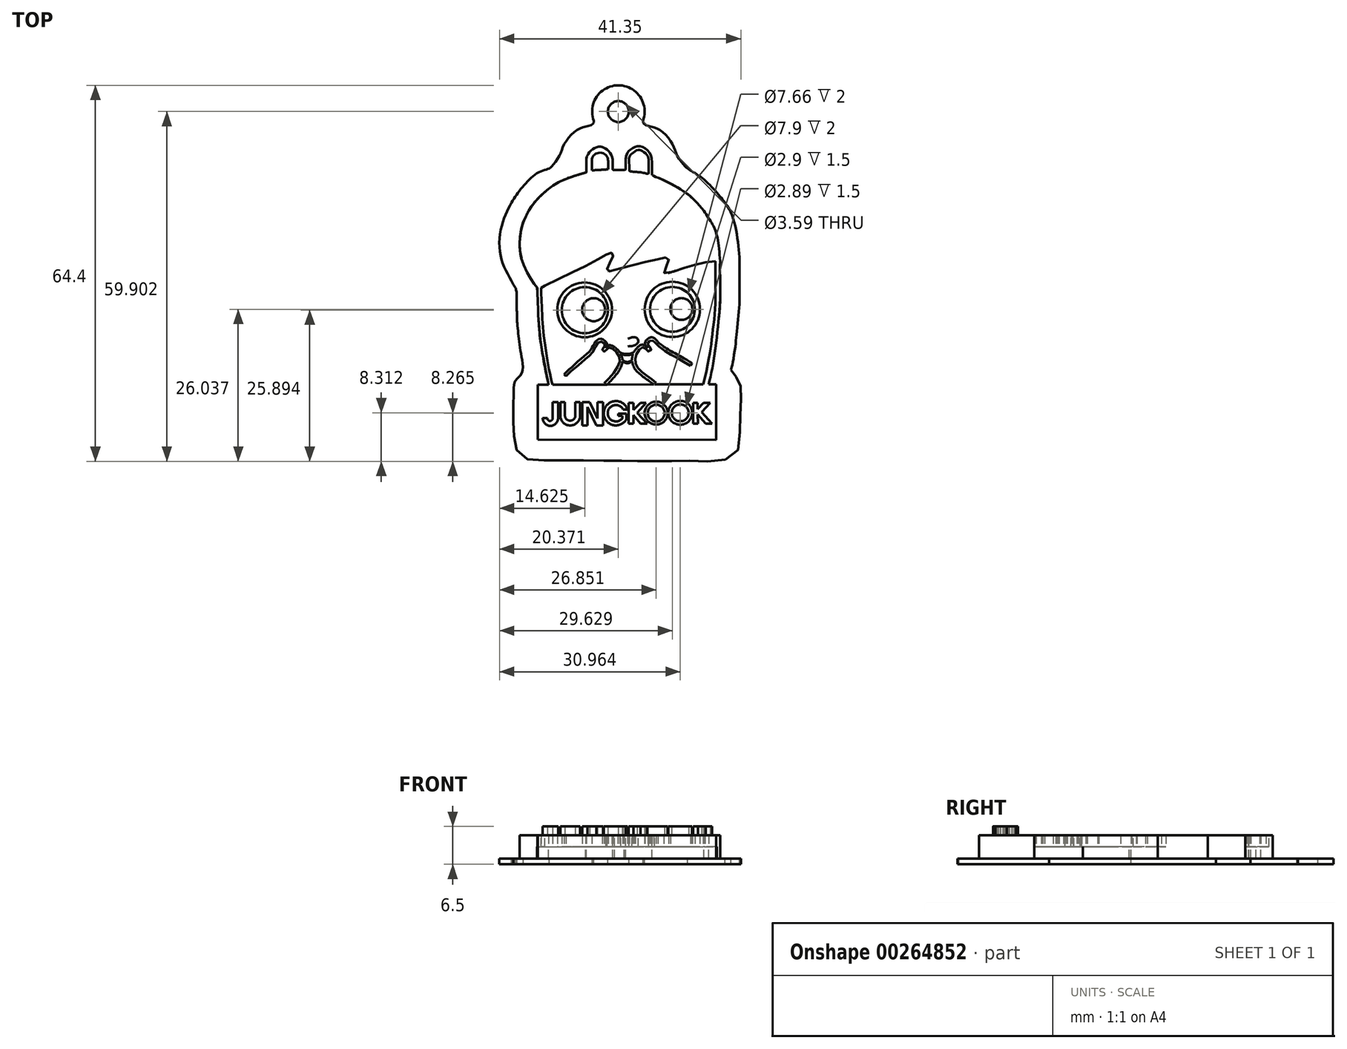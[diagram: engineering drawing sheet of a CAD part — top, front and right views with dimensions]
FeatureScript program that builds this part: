
annotation { "Feature Type Name" : "Feature", "Feature Type Description" : "" }
export const myFeature = defineFeature(function(context is Context, id is Id, definition is map)
    precondition{}
    {
        {
            var Q0;
            Q0=qCreatedBy(makeId("Top.planeOp"),FACE);
            var sketch = newSketch(context, id + "F0", { "sketchPlane" : qUnion([Q0])});
            skFitSpline(sketch, "E0", {"points": [v(-15.44, 3.8) * mm, v(-15.4, 3.06) * mm, v(-15.31, 1.12) * mm, v(-15.25, -0.63) * mm, v(-15.09, -3.15) * mm, v(-14.76, -5.82) * mm, v(-14.35, -8.3) * mm, v(-13.98, -10.2) * mm, v(-13.5, -12.48) * mm], "startDerivative": vector(0.66, -8.16) * mm, "endDerivative": vector(3.78, -17.47) * mm});
            skFitSpline(sketch, "E1", {"points": [v(-15.44, 3.8) * mm, v(-15.44, 4.09) * mm], "startDerivative": vector(0, 0.28) * mm, "endDerivative": vector(0, 0.28) * mm});
            skFitSpline(sketch, "E2", {"points": [v(-15.44, 4.09) * mm, v(-16.52, 5.66) * mm, v(-18.07, 8.9) * mm, v(-18.43, 11.83) * mm, v(-17.94, 15) * mm, v(-16.82, 17.42) * mm, v(-15.44, 19.28) * mm, v(-12.8, 21.53) * mm, v(-10.76, 22.67) * mm, v(-8.3, 23.5) * mm, v(-7.13, 23.85) * mm], "startDerivative": vector(-11.92, 16.14) * mm, "endDerivative": vector(15.07, 4.4) * mm});
            skFitSpline(sketch, "E3", {"points": [v(-7.13, 23.85) * mm, v(-7.03, 23.89) * mm, v(-7, 24.06) * mm], "startDerivative": vector(0.27, 0.05) * mm, "endDerivative": vector(0, 0.36) * mm});
            skFitSpline(sketch, "E4", {"points": [v(-7, 24.06) * mm, v(-7, 25.6) * mm, v(-7, 26.32) * mm], "startDerivative": vector(0, 2.86) * mm, "endDerivative": vector(0, 1.67) * mm});
            skFitSpline(sketch, "E5", {"points": [v(-7, 26.32) * mm, v(-6.88, 26.67) * mm, v(-6.59, 27.18) * mm, v(-5.88, 27.86) * mm, v(-5.1, 28.23) * mm, v(-4.41, 28.24) * mm, v(-3.8, 27.96) * mm, v(-3.14, 27.44) * mm, v(-2.64, 26.6) * mm, v(-2.5, 25.5) * mm], "startDerivative": vector(0.43, 2.5) * mm, "endDerivative": vector(0.33, -8.37) * mm});
            skFitSpline(sketch, "E6", {"points": [v(-2.5, 25.5) * mm, v(-2.5, 24.6) * mm], "startDerivative": vector(0, -0.9) * mm, "endDerivative": vector(0, -0.9) * mm});
            skFitSpline(sketch, "E7", {"points": [v(-2.5, 24.6) * mm, v(-2.45, 24.3) * mm, v(-2.22, 24.27) * mm], "startDerivative": vector(-0.02, -0.7) * mm, "endDerivative": vector(0.6, 0.05) * mm});
            skFitSpline(sketch, "E8", {"points": [v(-2.22, 24.27) * mm, v(-1.57, 24.27) * mm, v(-0.56, 24.27) * mm], "startDerivative": vector(1.37, 0) * mm, "endDerivative": vector(1.92, 0) * mm});
            skFitSpline(sketch, "E9", {"points": [v(-0.56, 24.27) * mm, v(-0.37, 24.31) * mm, v(-0.3, 24.69) * mm, v(-0.3, 25.35) * mm, v(-0.28, 26.2) * mm, v(0, 27.16) * mm, v(0.46, 27.7) * mm, v(0.96, 28.04) * mm, v(1.54, 28.27) * mm, v(2.25, 28.31) * mm, v(3.02, 27.97) * mm, v(3.65, 27.4) * mm, v(4.1, 26.52) * mm, v(4.2, 25.06) * mm, v(4.21, 23.66) * mm], "startDerivative": vector(6.4, 0.3) * mm, "endDerivative": vector(0.05, -13.65) * mm});
            skFitSpline(sketch, "E10", {"points": [v(4.21, 23.66) * mm, v(4.21, 23.5) * mm, v(4.44, 23.27) * mm, v(5.7, 22.76) * mm, v(7.7, 21.78) * mm, v(9.76, 20.54) * mm, v(11.37, 19.22) * mm, v(13.08, 17.27) * mm], "startDerivative": vector(-0.74, -3.46) * mm, "endDerivative": vector(8.63, -10.7) * mm});
            skFitSpline(sketch, "E11", {"points": [v(13.08, 17.27) * mm, v(14.13, 15.74) * mm, v(14.87, 14.38) * mm, v(15.47, 12.46) * mm, v(15.87, 8.68) * mm], "startDerivative": vector(4.76, -6.59) * mm, "endDerivative": vector(0.64, -11.93) * mm});
            skFitSpline(sketch, "E12", {"points": [v(15.87, 8.68) * mm, v(15.87, 5.96) * mm, v(15.87, 1.45) * mm, v(15.63, -1.38) * mm, v(15.33, -4.13) * mm], "startDerivative": vector(-0.06, -11.86) * mm, "endDerivative": vector(-1.6, -12.17) * mm});
            skFitSpline(sketch, "E13", {"points": [v(15.33, -4.13) * mm, v(15, -6.79) * mm, v(14.65, -9.15) * mm, v(14.27, -10.95) * mm, v(13.93, -12.45) * mm], "startDerivative": vector(-1, -9.39) * mm, "endDerivative": vector(-0.83, -6.4) * mm});
            skLineSegment(sketch, "E14", {"start": v(13.93, -12.45) * mm, "end": v(15.17, -12.45) * mm});
            skLineSegment(sketch, "E15", {"start": v(15.17, -12.45) * mm, "end": v(15.17, -21.93) * mm});
            skLineSegment(sketch, "E16", {"start": v(-15.34, -12.48) * mm, "end": v(-13.5, -12.48) * mm});
            skLineSegment(sketch, "E17", {"start": v(-15.34, -12.48) * mm, "end": v(-15.34, -21.89) * mm});
            skLineSegment(sketch, "E18", {"start": v(-15.34, -21.89) * mm, "end": v(15.17, -21.93) * mm});
            skSolve(sketch);
        }
        {
            var Q0;
            Q0=qCreatedBy(makeId("Top.planeOp"),FACE);
            cPlane(context, id + "F1", {"entities" : qUnion([Q0]), "cplaneType" : CPlaneType.OFFSET, "offset" : 0 * mm, "width" : 150 * mm, "height" : 150 * mm});
        }
        {
            var Q0;
            Q0=qCreatedBy(id+"F1.planeOp",FACE);
            var sketch = newSketch(context, id + "F2", { "sketchPlane" : qUnion([Q0])});
            skFitSpline(sketch, "E19", {"points": [v(-14.13, 4.47) * mm, v(-9.92, 6.48) * mm, v(-6.1, 8.41) * mm, v(-3.73, 9.74) * mm, v(-3.17, 10.02) * mm, v(-2.62, 10.07) * mm, v(-2.39, 9.9) * mm, v(-2.6, 9.24) * mm, v(-3.12, 8.1) * mm, v(-3.45, 7.46) * mm, v(-3.5, 6.94) * mm, v(-2.62, 7.05) * mm, v(0.59, 7.91) * mm, v(3.49, 8.62) * mm, v(6, 9.2) * mm, v(6.67, 9.3) * mm, v(7.04, 9.18) * mm, v(6.9, 8.26) * mm, v(6.35, 7.17) * mm, v(6.35, 6.61) * mm, v(8.36, 7.06) * mm, v(10.58, 7.76) * mm, v(13, 8.4) * mm, v(15.06, 8.68) * mm], "startDerivative": vector(54.67, 25.93) * mm, "endDerivative": vector(38.66, 5.37) * mm});
            skFitSpline(sketch, "E20", {"points": [v(-14.13, 4.47) * mm, v(-14.75, 4.08) * mm], "startDerivative": vector(-0.6, -0.38) * mm, "endDerivative": vector(-0.6, -0.38) * mm});
            skFitSpline(sketch, "E21", {"points": [v(-14.75, 4.08) * mm, v(-14.75, 2.53) * mm, v(-14.63, 0.52) * mm, v(-14.51, -2.05) * mm, v(-14.26, -4.55) * mm, v(-13.76, -7.92) * mm, v(-13.26, -10.61) * mm, v(-12.82, -12.49) * mm], "startDerivative": vector(-0.25, -12.97) * mm, "endDerivative": vector(3.26, -11.8) * mm});
            skFitSpline(sketch, "E22", {"points": [v(15.06, 8.68) * mm, v(15.06, 6.63) * mm, v(15.06, 4.57) * mm, v(15.06, 2.46) * mm, v(14.95, -0.47) * mm, v(14.67, -2.9) * mm, v(14.38, -5.36) * mm, v(14.03, -7.54) * mm, v(13.32, -11.25) * mm], "startDerivative": vector(0, -17.99) * mm, "endDerivative": vector(-4.99, -25.86) * mm});
            skPoint(sketch, "E23", {"position": v(13.93, -12.44) * mm});
            skFitSpline(sketch, "E24", {"points": [v(13.32, -11.25) * mm, v(13, -12.44) * mm], "startDerivative": vector(-0.32, -1.2) * mm, "endDerivative": vector(-0.32, -1.2) * mm});
            skLineSegment(sketch, "E25", {"start": v(13, -12.44) * mm, "end": v(13.93, -12.44) * mm});
            skFitSpline(sketch, "E26", {"points": [v(4.21, 23.66) * mm, v(4.21, 23.5) * mm, v(4.44, 23.27) * mm, v(5.7, 22.76) * mm, v(7.7, 21.78) * mm, v(9.76, 20.54) * mm, v(11.37, 19.22) * mm, v(13.08, 17.27) * mm], "startDerivative": vector(-0.95, -3.6) * mm, "endDerivative": vector(8.5, -10.78) * mm});
            skFitSpline(sketch, "E27", {"points": [v(13.08, 17.27) * mm, v(14.13, 15.75) * mm, v(14.87, 14.38) * mm, v(15.47, 12.46) * mm, v(15.87, 8.68) * mm], "startDerivative": vector(4.77, -6.59) * mm, "endDerivative": vector(0.64, -11.93) * mm});
            skFitSpline(sketch, "E28", {"points": [v(-0.56, 24.27) * mm, v(-0.37, 24.31) * mm, v(-0.3, 24.7) * mm, v(-0.3, 25.35) * mm, v(-0.27, 26.2) * mm, v(0, 27.16) * mm, v(0.46, 27.7) * mm, v(0.96, 28.04) * mm, v(1.54, 28.27) * mm, v(2.25, 28.31) * mm, v(3.02, 27.97) * mm, v(3.65, 27.4) * mm, v(4.1, 26.52) * mm, v(4.2, 25.06) * mm, v(4.21, 23.66) * mm], "startDerivative": vector(6.4, 0.3) * mm, "endDerivative": vector(0.05, -13.65) * mm});
            skFitSpline(sketch, "E29", {"points": [v(-2.22, 24.27) * mm, v(-1.58, 24.27) * mm, v(-0.56, 24.27) * mm], "startDerivative": vector(1.37, 0) * mm, "endDerivative": vector(1.92, 0) * mm});
            skFitSpline(sketch, "E30", {"points": [v(15.87, 8.68) * mm, v(15.87, 6.07) * mm, v(15.87, 1.62) * mm, v(15.63, -1.4) * mm, v(15.35, -4.16) * mm, v(15, -6.8) * mm, v(14.66, -9.15) * mm, v(14.27, -11.01) * mm, v(13.93, -12.44) * mm], "startDerivative": vector(-0.12, -19) * mm, "endDerivative": vector(-3.55, -14.78) * mm});
            skLineSegment(sketch, "E31", {"start": v(-12.82, -12.49) * mm, "end": v(-13.5, -12.49) * mm});
            skFitSpline(sketch, "E32", {"points": [v(-13.5, -12.49) * mm, v(-13.96, -10.2) * mm, v(-14.3, -8.3) * mm, v(-14.73, -5.88) * mm, v(-15.06, -3.1) * mm, v(-15.26, -0.63) * mm, v(-15.32, 1.18) * mm, v(-15.4, 3.06) * mm, v(-15.43, 3.8) * mm, v(-15.42, 4.08) * mm], "startDerivative": vector(-3.76, 18.3) * mm, "endDerivative": vector(0.73, 5.33) * mm});
            skFitSpline(sketch, "E33", {"points": [v(-15.42, 4.08) * mm, v(-16.52, 5.65) * mm, v(-18.06, 8.86) * mm, v(-18.43, 11.78) * mm, v(-17.97, 14.93) * mm, v(-16.85, 17.37) * mm, v(-15.42, 19.26) * mm, v(-12.82, 21.55) * mm, v(-10.7, 22.7) * mm, v(-8.29, 23.49) * mm, v(-7.13, 23.84) * mm], "startDerivative": vector(-12.12, 16.07) * mm, "endDerivative": vector(15.09, 4.7) * mm});
            skFitSpline(sketch, "E34", {"points": [v(-7.13, 23.84) * mm, v(-7.03, 23.89) * mm, v(-7, 24.06) * mm], "startDerivative": vector(0.27, 0.05) * mm, "endDerivative": vector(0, 0.37) * mm});
            skFitSpline(sketch, "E35", {"points": [v(-7, 24.06) * mm, v(-7, 25.6) * mm, v(-7, 26.31) * mm], "startDerivative": vector(0, 2.84) * mm, "endDerivative": vector(0, 1.59) * mm});
            skFitSpline(sketch, "E36", {"points": [v(-7, 26.31) * mm, v(-6.89, 26.66) * mm, v(-6.59, 27.2) * mm, v(-5.9, 27.86) * mm, v(-5.09, 28.23) * mm, v(-4.41, 28.23) * mm, v(-3.8, 27.96) * mm, v(-3.14, 27.44) * mm, v(-2.64, 26.61) * mm, v(-2.5, 25.5) * mm, v(-2.5, 24.6) * mm], "startDerivative": vector(1.28, 4.94) * mm, "endDerivative": vector(-0.09, -8.1) * mm});
            skFitSpline(sketch, "E37", {"points": [v(-2.5, 24.6) * mm, v(-2.46, 24.3) * mm, v(-2.22, 24.27) * mm], "startDerivative": vector(-0.04, -0.71) * mm, "endDerivative": vector(0.62, 0.05) * mm});
            skFitSpline(sketch, "E38", {"points": [v(-6.07, 24.2) * mm, v(-4.86, 24.28) * mm, v(-3.26, 24.4) * mm], "startDerivative": vector(2.24, 0.26) * mm, "endDerivative": vector(3.21, 0.23) * mm});
            skFitSpline(sketch, "E39", {"points": [v(-6.07, 24.2) * mm, v(-6.07, 25.28) * mm, v(-6.07, 26.17) * mm], "startDerivative": vector(0, 2.11) * mm, "endDerivative": vector(0, 1.87) * mm});
            skFitSpline(sketch, "E40", {"points": [v(-6.07, 26.17) * mm, v(-5.94, 26.53) * mm, v(-5.47, 27.02) * mm, v(-4.76, 27.23) * mm, v(-4.04, 27.1) * mm, v(-3.5, 26.62) * mm, v(-3.33, 26.17) * mm, v(-3.26, 25.56) * mm, v(-3.25, 24.94) * mm, v(-3.26, 24.4) * mm], "startDerivative": vector(0.93, 3.8) * mm, "endDerivative": vector(-0.03, -5.07) * mm});
            skFitSpline(sketch, "E41", {"points": [v(3.66, 24.08) * mm, v(3.67, 25.53) * mm, v(3.65, 26.13) * mm], "startDerivative": vector(-0.03, 2.7) * mm, "endDerivative": vector(-0.06, 1.38) * mm});
            skFitSpline(sketch, "E42", {"points": [v(3.65, 26.13) * mm, v(3.5, 26.57) * mm, v(3.08, 27.15) * mm, v(2.42, 27.6) * mm, v(2.05, 27.71) * mm, v(1.49, 27.6) * mm, v(0.92, 27.19) * mm, v(0.54, 26.85) * mm, v(0.3, 26.45) * mm, v(0.29, 25.6) * mm, v(0.33, 24.72) * mm, v(0.34, 24.3) * mm], "startDerivative": vector(-1.35, 5.39) * mm, "endDerivative": vector(0.1, -5.11) * mm});
            skFitSpline(sketch, "E43", {"points": [v(3.66, 24.08) * mm, v(3.66, 23.84) * mm], "startDerivative": vector(0, -0.24) * mm, "endDerivative": vector(0, -0.24) * mm});
            skFitSpline(sketch, "E44", {"points": [v(3.66, 23.84) * mm, v(3.6, 23.65) * mm, v(3.33, 23.66) * mm, v(2.44, 23.84) * mm, v(1.2, 23.98) * mm, v(0.55, 24.01) * mm, v(0.4, 24.08) * mm, v(0.34, 24.3) * mm], "startDerivative": vector(-0.37, -2.5) * mm, "endDerivative": vector(-0.33, 2.45) * mm});
            skSolve(sketch);
        }
        {
            var Q0;
            Q0=makeQuery(id+"F0.imprint","IMPRINT",FACE,{"disambiguationData":[TD([[makeQuery(id+"F0.imprint","IMPRINT",EDGE,{"derivedFrom":sQuery(id+"F0.wireOp",EDGE,"E0")}),1.0]])]});
            extrude(context, id + "F3", {"entities" : qUnion([Q0]), "oppositeDirection" : true, "depth" : 2 * mm, "offsetDistance" : 25 * mm});
        }
        {
            var Q0;
            Q0=makeQuery(id+"F2.imprint","IMPRINT",FACE,{"disambiguationData":[TD([[makeQuery(id+"F2.imprint","IMPRINT",EDGE,{"derivedFrom":sQuery(id+"F2.wireOp",EDGE,"E19")}),1.0]])]});
            extrude(context, id + "F4", {"entities" : qUnion([Q0]), "operationType" : NewBodyOperationType.ADD, "depth" : 2 * mm, "offsetDistance" : 25 * mm});
        }
        {
            var Q0;
            Q0=qCreatedBy(id+"F1.planeOp",FACE);
            var sketch = newSketch(context, id + "F5", { "sketchPlane" : qUnion([Q0])});
            skCircle(sketch, "E45", {"center": v(7.7, 0.4) * mm, "radius": 4.73 * mm});
            skPoint(sketch, "E45.first.point", {"position": v(7.75, 5.14) * mm});
            skPoint(sketch, "E45.second.point", {"position": v(7.73, -4.33) * mm});
            skPoint(sketch, "E45.third.point", {"position": v(2.97, 0.22) * mm});
            skCircle(sketch, "E46", {"center": v(7.72, 0.42) * mm, "radius": 3.83 * mm});
            skPoint(sketch, "E46.first.point", {"position": v(7.7, 4.25) * mm});
            skPoint(sketch, "E46.second.point", {"position": v(7.7, -3.42) * mm});
            skPoint(sketch, "E46.third.point", {"position": v(3.9, 0) * mm});
            skCircle(sketch, "E47", {"center": v(9.26, 0.47) * mm, "radius": 1.87 * mm});
            skPoint(sketch, "E47.first.point", {"position": v(9.38, 2.34) * mm});
            skPoint(sketch, "E47.second.point", {"position": v(9.27, -1.4) * mm});
            skPoint(sketch, "E47.third.point", {"position": v(7.39, 0.4) * mm});
            skCircle(sketch, "E48", {"center": v(-7.32, 0.33) * mm, "radius": 4.68 * mm});
            skPoint(sketch, "E48.first.point", {"position": v(-7.5, 5) * mm});
            skPoint(sketch, "E48.second.point", {"position": v(-7.31, -4.36) * mm});
            skPoint(sketch, "E48.third.point", {"position": v(-12, 0) * mm});
            skCircle(sketch, "E49", {"center": v(-7.29, 0.27) * mm, "radius": 3.95 * mm});
            skPoint(sketch, "E49.first.point", {"position": v(-7.42, 4.22) * mm});
            skPoint(sketch, "E49.second.point", {"position": v(-7.29, -3.68) * mm});
            skPoint(sketch, "E49.third.point", {"position": v(-3.34, 0.4) * mm});
            skCircle(sketch, "E50", {"center": v(-5.77, 0.35) * mm, "radius": 1.96 * mm});
            skPoint(sketch, "E50.first.point", {"position": v(-5.82, 2.31) * mm});
            skPoint(sketch, "E50.second.point", {"position": v(-5.7, -1.61) * mm});
            skPoint(sketch, "E50.third.point", {"position": v(-7.73, 0.27) * mm});
            skPoint(sketch, "E51", {"position": v(1.86, -5.14) * mm});
            skPoint(sketch, "E52", {"position": v(0.11, -5.14) * mm});
            skFitSpline(sketch, "E53", {"points": [v(0.11, -4.61) * mm, v(0.58, -4.43) * mm, v(0.9, -4.35) * mm, v(1.24, -4.34) * mm, v(1.55, -4.43) * mm, v(1.79, -4.68) * mm, v(1.86, -5.14) * mm, v(1.68, -5.46) * mm, v(1.22, -5.73) * mm, v(0.7, -5.88) * mm, v(0.11, -5.92) * mm], "startDerivative": vector(4.47, 1.78) * mm, "endDerivative": vector(-5.32, -0.17) * mm});
            skFitSpline(sketch, "E54.MirrorCS", {"points": [v(0.11, -4.61) * mm, v(-0.36, -4.43) * mm, v(-0.67, -4.35) * mm, v(-1.02, -4.34) * mm, v(-1.33, -4.43) * mm, v(-1.57, -4.68) * mm, v(-1.64, -5.14) * mm, v(-1.46, -5.46) * mm, v(-1, -5.73) * mm, v(-0.48, -5.88) * mm, v(0.11, -5.92) * mm], "startDerivative": vector(-4.47, 1.78) * mm, "endDerivative": vector(5.32, -0.17) * mm});
            skFitSpline(sketch, "E55", {"points": [v(-10.84, -10.68) * mm, v(-9.58, -9.53) * mm, v(-7.72, -7.87) * mm, v(-6.48, -6.82) * mm, v(-5.98, -6.03) * mm, v(-5.6, -5.33) * mm, v(-5.27, -4.93) * mm, v(-4.61, -4.62) * mm, v(-3.87, -4.92) * mm, v(-3.53, -5.45) * mm, v(-3.48, -5.86) * mm, v(-4, -6.5) * mm], "startDerivative": vector(9.78, 8.96) * mm, "endDerivative": vector(-6.85, -6.95) * mm});
            skFitSpline(sketch, "E56", {"points": [v(-4, -6.5) * mm, v(-3.4, -5.87) * mm], "startDerivative": vector(0.65, 0.68) * mm, "endDerivative": vector(0.65, 0.68) * mm});
            skFitSpline(sketch, "E57", {"points": [v(-3.4, -5.87) * mm, v(-3.06, -5.72) * mm, v(-2.22, -6.05) * mm, v(-1.32, -6.92) * mm, v(-0.87, -7.94) * mm, v(-0.94, -9.08) * mm, v(-2.08, -10.98) * mm, v(-3.48, -12.51) * mm], "startDerivative": vector(2.61, 2.7) * mm, "endDerivative": vector(-7.54, -8.85) * mm});
            skLineSegment(sketch, "E58", {"start": v(-10.54, -11.04) * mm, "end": v(-10.84, -10.68) * mm});
            skFitSpline(sketch, "E59", {"points": [v(-10.54, -11.04) * mm, v(-9.27, -9.87) * mm, v(-8.06, -8.86) * mm, v(-7.28, -8.18) * mm, v(-6.45, -7.49) * mm, v(-5.87, -6.8) * mm, v(-5.32, -5.72) * mm, v(-5, -5.29) * mm, v(-4.58, -5.11) * mm, v(-4.12, -5.25) * mm, v(-3.84, -5.58) * mm, v(-3.86, -5.85) * mm, v(-4.23, -6.3) * mm, v(-4.25, -6.74) * mm, v(-3.85, -6.78) * mm, v(-3.48, -6.44) * mm, v(-3.25, -6.18) * mm, v(-3.03, -6.13) * mm, v(-2.64, -6.27) * mm, v(-2.04, -6.77) * mm, v(-1.4, -7.65) * mm, v(-1.3, -8.48) * mm, v(-1.72, -9.55) * mm, v(-2.82, -11.04) * mm, v(-3.97, -12.23) * mm], "startDerivative": vector(19.99, 19.03) * mm, "endDerivative": vector(-18.92, -18.35) * mm});
            skLineSegment(sketch, "E60", {"start": v(-3.48, -12.51) * mm, "end": v(-3.97, -12.23) * mm});
            skFitSpline(sketch, "E61", {"points": [v(4.6, -12.5) * mm, v(3.4, -11.64) * mm, v(2.02, -10.58) * mm, v(1.19, -9.6) * mm, v(0.82, -8.28) * mm, v(1.04, -7.07) * mm, v(1.98, -5.9) * mm, v(2.72, -5.66) * mm, v(3.49, -6.2) * mm], "startDerivative": vector(-8.33, 6.54) * mm, "endDerivative": vector(7.03, -7.38) * mm});
            skFitSpline(sketch, "E62", {"points": [v(5.26, -5.2) * mm, v(4.7, -4.6) * mm, v(4.06, -4.4) * mm, v(3.2, -4.91) * mm, v(3.06, -5.63) * mm, v(3.49, -6.2) * mm], "startDerivative": vector(-2.5, 2.63) * mm, "endDerivative": vector(2.54, -3.64) * mm});
            skFitSpline(sketch, "E63", {"points": [v(5.26, -5.2) * mm, v(6.24, -5.98) * mm, v(7.83, -6.95) * mm, v(9.85, -8.07) * mm, v(11.1, -8.79) * mm], "startDerivative": vector(4.6, -3.9) * mm, "endDerivative": vector(5, -2.96) * mm});
            skLineSegment(sketch, "E64", {"start": v(11.1, -8.79) * mm, "end": v(10.83, -9.27) * mm});
            skFitSpline(sketch, "E65", {"points": [v(4.93, -12.14) * mm, v(3.68, -11.2) * mm, v(2.41, -10.26) * mm, v(1.6, -9.25) * mm, v(1.34, -8.24) * mm, v(1.54, -7.3) * mm, v(2.23, -6.3) * mm, v(2.76, -6.1) * mm, v(3.19, -6.42) * mm, v(3.64, -6.82) * mm, v(4.07, -6.53) * mm, v(3.8, -5.96) * mm, v(3.49, -5.61) * mm, v(3.65, -5.19) * mm, v(4.06, -4.89) * mm, v(4.56, -5.11) * mm, v(4.93, -5.5) * mm, v(6.59, -6.82) * mm, v(8.43, -7.85) * mm, v(10.83, -9.27) * mm], "startDerivative": vector(-17.76, 13.97) * mm, "endDerivative": vector(29.25, -15.47) * mm});
            skLineSegment(sketch, "E66", {"start": v(4.93, -12.14) * mm, "end": v(4.6, -12.5) * mm});
            skFitSpline(sketch, "E67", {"points": [v(-1.32, -6.92) * mm, v(-0.73, -7.17) * mm, v(0, -7.23) * mm], "startDerivative": vector(1.15, -0.55) * mm, "endDerivative": vector(1.45, -0.09) * mm});
            skFitSpline(sketch, "E68", {"points": [v(0, -7.23) * mm, v(0.52, -7.17) * mm, v(1.11, -6.92) * mm], "startDerivative": vector(1.08, 0.03) * mm, "endDerivative": vector(1.14, 0.58) * mm});
            skFitSpline(sketch, "E69", {"points": [v(-0.83, -8.47) * mm, v(-0.48, -8.71) * mm, v(0, -8.8) * mm], "startDerivative": vector(0.7, -0.4) * mm, "endDerivative": vector(0.95, -0.05) * mm});
            skFitSpline(sketch, "E70", {"points": [v(0, -8.8) * mm, v(0.43, -8.71) * mm, v(0.84, -8.47) * mm], "startDerivative": vector(0.88, 0.07) * mm, "endDerivative": vector(0.8, 0.38) * mm});
            skFitSpline(sketch, "E71", {"points": [v(0, -7.43) * mm, v(0.54, -7.36) * mm, v(0.98, -7.2) * mm], "startDerivative": vector(1.07, 0.1) * mm, "endDerivative": vector(0.9, 0.37) * mm});
            skFitSpline(sketch, "E72", {"points": [v(0, -7.43) * mm, v(-0.73, -7.36) * mm, v(-1.13, -7.23) * mm], "startDerivative": vector(-1.38, 0.08) * mm, "endDerivative": vector(-0.86, 0.33) * mm});
            skFitSpline(sketch, "E73", {"points": [v(0, -8.6) * mm, v(0.4, -8.5) * mm, v(0.82, -8.25) * mm], "startDerivative": vector(0.85, 0.15) * mm, "endDerivative": vector(0.78, 0.55) * mm});
            skFitSpline(sketch, "E74", {"points": [v(0, -8.6) * mm, v(-0.44, -8.5) * mm, v(-0.83, -8.25) * mm], "startDerivative": vector(-0.92, 0.14) * mm, "endDerivative": vector(-0.75, 0.57) * mm});
            skSolve(sketch);
        }
        {
            var Q0;
            Q0 = qSketchRegion(id + "F5", true);
            extrude(context, id + "F6", {"entities" : qUnion([Q0]), "operationType" : NewBodyOperationType.ADD, "depth" : 2 * mm, "offsetDistance" : 25 * mm});
        }
        {
            var Q0;
            Q0=makeQuery(id+"F5.imprint","IMPRINT",FACE,{"disambiguationData":[TD([[makeQuery(id+"F5.imprint","IMPRINT",EDGE,{"derivedFrom":sQuery(id+"F5.wireOp",EDGE,"E50")}),1.0]])]});
            var Q1;
            Q1=makeQuery(id+"F5.imprint","IMPRINT",FACE,{"disambiguationData":[TD([[makeQuery(id+"F5.imprint","IMPRINT",EDGE,{"derivedFrom":sQuery(id+"F5.wireOp",EDGE,"E47")}),1.0]])]});
            extrude(context, id + "F7", {"entities" : qUnion([Q0, Q1]), "operationType" : NewBodyOperationType.ADD, "depth" : 2 * mm, "offsetDistance" : 25 * mm});
        }
        {
            var Q0;
            Q0=qCreatedBy(id+"F1.planeOp",FACE);
            var sketch = newSketch(context, id + "F8", { "sketchPlane" : qUnion([Q0])});
            skPoint(sketch, "E75", {"position": v(-15.34, -12.48) * mm});
            skLineSegment(sketch, "E76.0", {"start": v(-15.34, -12.48) * mm, "end": v(-15.34, -21.89) * mm});
            skPoint(sketch, "E77", {"position": v(-12.82, -12.49) * mm});
            skPoint(sketch, "E78", {"position": v(13, -12.44) * mm});
            skPoint(sketch, "E79", {"position": v(15.17, -12.45) * mm});
            skPoint(sketch, "E80", {"position": v(15.17, -21.93) * mm});
            skPoint(sketch, "E81", {"position": v(-15.34, -21.89) * mm});
            skLineSegment(sketch, "E82", {"start": v(-12.82, -12.49) * mm, "end": v(-15.34, -12.48) * mm});
            skLineSegment(sketch, "E83", {"start": v(-15.34, -21.89) * mm, "end": v(15.17, -21.93) * mm});
            skLineSegment(sketch, "E84", {"start": v(15.17, -12.45) * mm, "end": v(15.17, -21.93) * mm});
            skLineSegment(sketch, "E85", {"start": v(15.17, -12.45) * mm, "end": v(13, -12.44) * mm});
            skLineSegment(sketch, "E86", {"start": v(-12.82, -12.49) * mm, "end": v(13, -12.44) * mm});
            skSolve(sketch);
        }
        {
            var Q0;
            Q0=makeQuery(id+"F8.imprint","IMPRINT",FACE,{"disambiguationData":[TD([[makeQuery(id+"F8.imprint","IMPRINT",EDGE,{"derivedFrom":sQuery(id+"F8.wireOp",EDGE,"E76.0")}),1.0]])]});
            extrude(context, id + "F9", {"entities" : qUnion([Q0]), "operationType" : NewBodyOperationType.ADD, "depth" : 2 * mm, "offsetDistance" : 25 * mm});
        }
        {
            var Q0;
            Q0=makeQuery(id+"F9.boolean.opBoolean","MERGE",FACE,{"derivedFrom":[makeQuery(id+"F4.opExtrude","CAP_FACE",FACE,{"disambiguationData":[OSD([sQuery(id+"F2.wireOp",EDGE,"E19"),sQuery(id+"F2.wireOp",EDGE,"E20"),sQuery(id+"F2.wireOp",EDGE,"E21"),sQuery(id+"F2.wireOp",EDGE,"E22"),sQuery(id+"F2.wireOp",EDGE,"E24"),sQuery(id+"F2.wireOp",EDGE,"E25"),sQuery(id+"F2.wireOp",EDGE,"E26"),sQuery(id+"F2.wireOp",EDGE,"E27"),sQuery(id+"F2.wireOp",EDGE,"E28"),sQuery(id+"F2.wireOp",EDGE,"E29"),sQuery(id+"F2.wireOp",EDGE,"E30"),sQuery(id+"F2.wireOp",EDGE,"E31"),sQuery(id+"F2.wireOp",EDGE,"E32"),sQuery(id+"F2.wireOp",EDGE,"E33"),sQuery(id+"F2.wireOp",EDGE,"E34"),sQuery(id+"F2.wireOp",EDGE,"E35"),sQuery(id+"F2.wireOp",EDGE,"E36"),sQuery(id+"F2.wireOp",EDGE,"E37"),sQuery(id+"F2.wireOp",EDGE,"E38"),sQuery(id+"F2.wireOp",EDGE,"E39"),sQuery(id+"F2.wireOp",EDGE,"E40"),sQuery(id+"F2.wireOp",EDGE,"E41"),sQuery(id+"F2.wireOp",EDGE,"E42"),sQuery(id+"F2.wireOp",EDGE,"E43"),sQuery(id+"F2.wireOp",EDGE,"E44")])],"isStart":false}),makeQuery(id+"F6.opExtrude","CAP_FACE",FACE,{"disambiguationData":[OSD([sQuery(id+"F5.wireOp",EDGE,"E55"),sQuery(id+"F5.wireOp",EDGE,"E56"),sQuery(id+"F5.wireOp",EDGE,"E57"),sQuery(id+"F5.wireOp",EDGE,"E58"),sQuery(id+"F5.wireOp",EDGE,"E59"),sQuery(id+"F5.wireOp",EDGE,"E60"),sQuery(id+"F5.wireOp",EDGE,"E61"),sQuery(id+"F5.wireOp",EDGE,"E62"),sQuery(id+"F5.wireOp",EDGE,"E63"),sQuery(id+"F5.wireOp",EDGE,"E64"),sQuery(id+"F5.wireOp",EDGE,"E65"),sQuery(id+"F5.wireOp",EDGE,"E66"),sQuery(id+"F5.wireOp",EDGE,"E67"),sQuery(id+"F5.wireOp",EDGE,"E68"),sQuery(id+"F5.wireOp",EDGE,"E69"),sQuery(id+"F5.wireOp",EDGE,"E70"),sQuery(id+"F5.wireOp",EDGE,"E71"),sQuery(id+"F5.wireOp",EDGE,"E72"),sQuery(id+"F5.wireOp",EDGE,"E73"),sQuery(id+"F5.wireOp",EDGE,"E74")])],"isStart":false}),makeQuery(id+"F9.opExtrude","CAP_FACE",FACE,{"disambiguationData":[OSD([sQuery(id+"F8.wireOp",EDGE,"E76.0"),sQuery(id+"F8.wireOp",EDGE,"E82"),sQuery(id+"F8.wireOp",EDGE,"E83"),sQuery(id+"F8.wireOp",EDGE,"E84"),sQuery(id+"F8.wireOp",EDGE,"E85"),sQuery(id+"F8.wireOp",EDGE,"E86")])],"isStart":false})]});
            var sketch = newSketch(context, id + "F10", { "sketchPlane" : qUnion([Q0])});
            skLineSegment(sketch, "E87", {"start": v(-12.78, -15.45) * mm, "end": v(-11.86, -15.45) * mm});
            skLineSegment(sketch, "E88", {"start": v(-11.86, -15.45) * mm, "end": v(-11.86, -18.22) * mm});
            skLineSegment(sketch, "E89", {"start": v(-12.78, -15.45) * mm, "end": v(-12.78, -18.22) * mm});
            skLineSegment(sketch, "E90", {"start": v(-14.5, -18.22) * mm, "end": v(-13.72, -18.22) * mm});
            skLineSegment(sketch, "E91", {"start": v(-8.91, -15.45) * mm, "end": v(-8.09, -15.45) * mm});
            skLineSegment(sketch, "E92", {"start": v(-10.69, -15.45) * mm, "end": v(-11.5, -15.45) * mm});
            skLineSegment(sketch, "E93", {"start": v(-11.5, -15.45) * mm, "end": v(-11.5, -17.77) * mm});
            skLineSegment(sketch, "E94", {"start": v(-10.69, -15.45) * mm, "end": v(-10.69, -17.77) * mm});
            skLineSegment(sketch, "E95", {"start": v(-8.09, -15.45) * mm, "end": v(-8.09, -17.77) * mm});
            skLineSegment(sketch, "E96", {"start": v(-8.91, -15.45) * mm, "end": v(-8.91, -17.77) * mm});
            skArc(sketch, "E97", {"start": v(-11.5, -17.77) * mm, "mid": v(-9.8, -19.47) * mm, "end": v(-8.09, -17.77) * mm});
            skArc(sketch, "E98", {"start": v(-10.69, -17.77) * mm, "mid": v(-9.8, -18.66) * mm, "end": v(-8.91, -17.77) * mm});
            skArc(sketch, "E99", {"start": v(-11.86, -18.22) * mm, "mid": v(-13.18, -19.54) * mm, "end": v(-14.5, -18.22) * mm});
            skArc(sketch, "E100", {"start": v(-12.78, -18.22) * mm, "mid": v(-13.25, -18.7) * mm, "end": v(-13.72, -18.22) * mm});
            skLineSegment(sketch, "E101", {"start": v(-7.71, -15.45) * mm, "end": v(-7.71, -19.47) * mm});
            skPoint(sketch, "E101.endSnap0", {"position": v(-9.8, -19.47) * mm});
            skLineSegment(sketch, "E102", {"start": v(-7.71, -19.47) * mm, "end": v(-6.84, -19.47) * mm});
            skLineSegment(sketch, "E103", {"start": v(-6.84, -19.47) * mm, "end": v(-6.84, -16.32) * mm});
            skLineSegment(sketch, "E104", {"start": v(-7.71, -15.45) * mm, "end": v(-6.44, -15.45) * mm});
            skLineSegment(sketch, "E105", {"start": v(-6.44, -15.45) * mm, "end": v(-5.14, -18.3) * mm});
            skLineSegment(sketch, "E106", {"start": v(-5.14, -18.3) * mm, "end": v(-5.14, -15.45) * mm});
            skLineSegment(sketch, "E107", {"start": v(-5.14, -15.45) * mm, "end": v(-4.19, -15.45) * mm});
            skLineSegment(sketch, "E108", {"start": v(-4.19, -15.45) * mm, "end": v(-4.19, -19.5) * mm});
            skLineSegment(sketch, "E109", {"start": v(-4.19, -19.5) * mm, "end": v(-5.33, -19.5) * mm});
            skLineSegment(sketch, "E110", {"start": v(-5.33, -19.5) * mm, "end": v(-6.84, -16.32) * mm});
            skLineSegment(sketch, "E111", {"start": v(0.2, -15.6) * mm, "end": v(1.07, -15.6) * mm});
            skLineSegment(sketch, "E112", {"start": v(1.07, -15.6) * mm, "end": v(1.07, -16.84) * mm});
            skLineSegment(sketch, "E113", {"start": v(1.07, -16.84) * mm, "end": v(2.25, -15.6) * mm});
            skLineSegment(sketch, "E114", {"start": v(2.25, -15.6) * mm, "end": v(3.2, -15.6) * mm});
            skLineSegment(sketch, "E115", {"start": v(3.2, -15.6) * mm, "end": v(1.65, -17.3) * mm});
            skLineSegment(sketch, "E116", {"start": v(1.65, -17.3) * mm, "end": v(3.4, -19.18) * mm});
            skLineSegment(sketch, "E117", {"start": v(3.4, -19.18) * mm, "end": v(2.26, -19.18) * mm});
            skLineSegment(sketch, "E118", {"start": v(2.26, -19.18) * mm, "end": v(1.07, -17.67) * mm});
            skLineSegment(sketch, "E119", {"start": v(1.07, -17.67) * mm, "end": v(1.07, -19.18) * mm});
            skLineSegment(sketch, "E120", {"start": v(1.07, -19.18) * mm, "end": v(0.2, -19.18) * mm});
            skLineSegment(sketch, "E121", {"start": v(0.2, -19.18) * mm, "end": v(0.2, -15.6) * mm});
            skCircle(sketch, "E122", {"center": v(4.94, -17.35) * mm, "radius": 1.97 * mm});
            skPoint(sketch, "E122.first.point", {"position": v(4.95, -15.38) * mm});
            skPoint(sketch, "E122.second.point", {"position": v(5.14, -19.32) * mm});
            skPoint(sketch, "E122.third.point", {"position": v(6.89, -17.06) * mm});
            skCircle(sketch, "E123", {"center": v(9.05, -17.3) * mm, "radius": 2.04 * mm});
            skPoint(sketch, "E123.first.point", {"position": v(8.85, -15.28) * mm});
            skPoint(sketch, "E123.second.point", {"position": v(9.15, -19.35) * mm});
            skPoint(sketch, "E123.third.point", {"position": v(11.08, -17.58) * mm});
            skPoint(sketch, "E124.first.point", {"position": v(4.95, -15.9) * mm});
            skPoint(sketch, "E124.third.point", {"position": v(6.39, -17.35) * mm});
            skCircle(sketch, "E125", {"center": v(9.05, -17.3) * mm, "radius": 1.45 * mm});
            skCircle(sketch, "E126", {"center": v(4.94, -17.35) * mm, "radius": 1.45 * mm});
            skLineSegment(sketch, "E127", {"start": v(11.28, -19.18) * mm, "end": v(12.09, -19.16) * mm});
            skLineSegment(sketch, "E128", {"start": v(12.09, -19.16) * mm, "end": v(12.05, -17.56) * mm});
            skLineSegment(sketch, "E129", {"start": v(12.05, -17.56) * mm, "end": v(13.44, -19.18) * mm});
            skLineSegment(sketch, "E130", {"start": v(13.44, -19.18) * mm, "end": v(14.52, -19.16) * mm});
            skLineSegment(sketch, "E131", {"start": v(14.52, -19.16) * mm, "end": v(12.7, -17.19) * mm});
            skLineSegment(sketch, "E132", {"start": v(12.7, -17.19) * mm, "end": v(14.21, -15.6) * mm});
            skLineSegment(sketch, "E133", {"start": v(14.21, -15.6) * mm, "end": v(13.07, -15.58) * mm});
            skLineSegment(sketch, "E134", {"start": v(13.07, -15.58) * mm, "end": v(12.05, -16.7) * mm});
            skLineSegment(sketch, "E135", {"start": v(12.05, -16.7) * mm, "end": v(12.05, -15.6) * mm});
            skLineSegment(sketch, "E136", {"start": v(12.05, -15.6) * mm, "end": v(11.28, -15.58) * mm});
            skLineSegment(sketch, "E137", {"start": v(11.28, -15.58) * mm, "end": v(11.28, -19.18) * mm});
            skArc(sketch, "E138", {"start": v(-0.2, -16.28) * mm, "mid": v(-4.05, -17.28) * mm, "end": v(-0.3, -18.62) * mm});
            skFitSpline(sketch, "E139", {"points": [v(-0.3, -18.62) * mm, v(-0.2, -18.45) * mm, v(-0.15, -18.22) * mm], "startDerivative": vector(0.19, 0.22) * mm, "endDerivative": vector(-0.03, 0.5) * mm});
            skArc(sketch, "E140", {"start": v(-0.85, -18.22) * mm, "mid": v(-3.36, -17.25) * mm, "end": v(-0.71, -16.74) * mm});
            skLineSegment(sketch, "E141", {"start": v(-0.71, -16.74) * mm, "end": v(0, -16.74) * mm});
            skFitSpline(sketch, "E142", {"points": [v(-0.2, -16.28) * mm, v(0, -16.74) * mm], "startDerivative": vector(0.2, -0.46) * mm, "endDerivative": vector(0.2, -0.46) * mm});
            skLineSegment(sketch, "E143", {"start": v(-0.85, -18.22) * mm, "end": v(-0.85, -17.85) * mm});
            skLineSegment(sketch, "E144", {"start": v(-0.85, -17.85) * mm, "end": v(-1.55, -17.85) * mm});
            skLineSegment(sketch, "E145", {"start": v(-1.55, -17.85) * mm, "end": v(-1.55, -17.43) * mm});
            skLineSegment(sketch, "E146", {"start": v(-1.55, -17.43) * mm, "end": v(-0.15, -17.43) * mm});
            skLineSegment(sketch, "E147", {"start": v(-0.15, -17.43) * mm, "end": v(-0.15, -18.22) * mm});
            skSolve(sketch);
        }
        {
            var Q0;
            Q0 = qSketchRegion(id + "F10", true);
            extrude(context, id + "F11", {"entities" : qUnion([Q0]), "operationType" : NewBodyOperationType.ADD, "depth" : 1.5 * mm, "offsetDistance" : 25 * mm});
        }
        {
            var Q0;
            Q0=makeQuery(id+"F3.opExtrude","CAP_FACE",FACE,{"disambiguationData":[OSD([sQuery(id+"F0.wireOp",EDGE,"E0"),sQuery(id+"F0.wireOp",EDGE,"E1"),sQuery(id+"F0.wireOp",EDGE,"E2"),sQuery(id+"F0.wireOp",EDGE,"E3"),sQuery(id+"F0.wireOp",EDGE,"E4"),sQuery(id+"F0.wireOp",EDGE,"E5"),sQuery(id+"F0.wireOp",EDGE,"E6"),sQuery(id+"F0.wireOp",EDGE,"E7"),sQuery(id+"F0.wireOp",EDGE,"E8"),sQuery(id+"F0.wireOp",EDGE,"E9"),sQuery(id+"F0.wireOp",EDGE,"E10"),sQuery(id+"F0.wireOp",EDGE,"E11"),sQuery(id+"F0.wireOp",EDGE,"E12"),sQuery(id+"F0.wireOp",EDGE,"E13"),sQuery(id+"F0.wireOp",EDGE,"E14"),sQuery(id+"F0.wireOp",EDGE,"E15"),sQuery(id+"F0.wireOp",EDGE,"E16"),sQuery(id+"F0.wireOp",EDGE,"E17"),sQuery(id+"F0.wireOp",EDGE,"E18")])],"isStart":false});
            var sketch = newSketch(context, id + "F12", { "sketchPlane" : qUnion([Q0])});
            skArc(sketch, "E148", {"start": v(-5.75, -32.7) * mm, "mid": v(-1.48, -38.78) * mm, "end": v(2.63, -32.6) * mm});
            skCircle(sketch, "E149", {"center": v(-1.54, -34.28) * mm, "radius": 1.8 * mm});
            skFitSpline(sketch, "E150", {"points": [v(-5.75, -32.7) * mm, v(-5.9, -32.2) * mm, v(-7.1, -31.7) * mm, v(-9.02, -30.86) * mm, v(-10.92, -28.47) * mm, v(-11.66, -26.65) * mm, v(-12.95, -24.88) * mm, v(-13.37, -24.53) * mm], "startDerivative": vector(-0.7, 6.25) * mm, "endDerivative": vector(-9.08, 6.6) * mm});
            skLineSegment(sketch, "E151", {"start": v(-1.54, -49.33) * mm, "end": v(-1.54, -16.28) * mm, "construction": true});
            skFitSpline(sketch, "E152.MirrorCS", {"points": [v(2.67, -32.7) * mm, v(2.81, -32.2) * mm, v(4.02, -31.7) * mm, v(5.94, -30.86) * mm, v(7.84, -28.47) * mm, v(8.59, -26.65) * mm, v(9.88, -24.88) * mm, v(10.3, -24.53) * mm], "startDerivative": vector(0.7, 6.25) * mm, "endDerivative": vector(9.08, 6.6) * mm});
            skFitSpline(sketch, "E153", {"points": [v(-13.37, -24.53) * mm, v(-15.34, -23.8) * mm, v(-17.94, -21.38) * mm, v(-19.82, -18.66) * mm], "startDerivative": vector(-5.25, 2.15) * mm, "endDerivative": vector(-4.3, 8.35) * mm});
            skLineSegment(sketch, "E154", {"start": v(-1.54, -16.28) * mm, "end": v(-1.54, 4.94) * mm, "construction": true});
            skPoint(sketch, "E155", {"position": v(-20.87, -16.61) * mm});
            skPoint(sketch, "E156", {"position": v(-21.76, -13.59) * mm});
            skPoint(sketch, "E157", {"position": v(-21.76, -9.83) * mm});
            skPoint(sketch, "E158", {"position": v(-20.73, -6.92) * mm});
            skPoint(sketch, "E159", {"position": v(-19.18, -4.09) * mm});
            skFitSpline(sketch, "E160", {"points": [v(-19.82, -18.66) * mm, v(-20.87, -16.61) * mm, v(-21.76, -13.59) * mm, v(-21.76, -9.83) * mm, v(-20.73, -6.92) * mm, v(-19.18, -4.09) * mm], "startDerivative": vector(-6.72, 9.79) * mm, "endDerivative": vector(7.86, 13.7) * mm});
            skPoint(sketch, "E161", {"position": v(17.97, -16.37) * mm});
            skPoint(sketch, "E162", {"position": v(18.72, -13.44) * mm});
            skPoint(sketch, "E163", {"position": v(19.11, -10.33) * mm});
            skPoint(sketch, "E164", {"position": v(19.2, -7.46) * mm});
            skPoint(sketch, "E165", {"position": v(19.2, -3.62) * mm});
            skFitSpline(sketch, "E166", {"points": [v(16.74, -18.66) * mm, v(17.97, -16.37) * mm, v(18.72, -13.44) * mm, v(19.11, -10.33) * mm, v(19.2, -7.46) * mm, v(19.2, -3.62) * mm], "startDerivative": vector(8.65, 11.86) * mm, "endDerivative": vector(0.7, 16.32) * mm});
            skPoint(sketch, "E167", {"position": v(19.2, -1.4) * mm});
            skPoint(sketch, "E168", {"position": v(18.95, 1.43) * mm});
            skPoint(sketch, "E169", {"position": v(18.65, 4.13) * mm});
            skPoint(sketch, "E170", {"position": v(17.74, 9.92) * mm});
            skPoint(sketch, "E171", {"position": v(18.05, 8.63) * mm});
            skPoint(sketch, "E172", {"position": v(18.5, 5.86) * mm});
            skPoint(sketch, "E173", {"position": v(-19.02, -3.62) * mm});
            skPoint(sketch, "E174", {"position": v(-18.97, -2.55) * mm});
            skPoint(sketch, "E175", {"position": v(-18.96, -1.2) * mm});
            skPoint(sketch, "E176", {"position": v(-18.92, 0.42) * mm});
            skPoint(sketch, "E177", {"position": v(-18.82, 2.4) * mm});
            skFitSpline(sketch, "E178", {"points": [v(19.2, -3.62) * mm, v(19.2, -1.4) * mm, v(18.95, 1.43) * mm, v(18.65, 4.13) * mm, v(18.5, 5.86) * mm, v(18.05, 8.63) * mm, v(17.74, 9.92) * mm], "startDerivative": vector(0.6, 13.27) * mm, "endDerivative": vector(-3.8, 12.5) * mm});
            skFitSpline(sketch, "E179", {"points": [v(10.3, -24.53) * mm, v(11.4, -23.84) * mm, v(13.35, -22.46) * mm, v(15.4, -20.33) * mm, v(16.74, -18.66) * mm], "startDerivative": vector(5.14, 3.25) * mm, "endDerivative": vector(5.29, 6.51) * mm});
            skFitSpline(sketch, "E180", {"points": [v(-19.18, -4.09) * mm, v(-19.02, -3.62) * mm, v(-18.97, -2.55) * mm, v(-18.96, -1.2) * mm, v(-18.92, 0.42) * mm, v(-18.82, 2.4) * mm], "startDerivative": vector(1.51, 3.32) * mm, "endDerivative": vector(0.97, 8.9) * mm});
            skPoint(sketch, "E181", {"position": v(-17.98, 8.43) * mm});
            skPoint(sketch, "E182", {"position": v(-17.95, 10.07) * mm});
            skPoint(sketch, "E183", {"position": v(-18.46, 11.06) * mm});
            skPoint(sketch, "E184", {"position": v(-19.23, 11.9) * mm});
            skPoint(sketch, "E185", {"position": v(-19.48, 13.83) * mm});
            skPoint(sketch, "E186", {"position": v(-19.55, 16.03) * mm});
            skPoint(sketch, "E187", {"position": v(-19.52, 18.88) * mm});
            skPoint(sketch, "E188", {"position": v(-17.47, 25.14) * mm});
            skPoint(sketch, "E189", {"position": v(-14.48, 25.45) * mm});
            skPoint(sketch, "E190", {"position": v(-10.38, 25.45) * mm});
            skPoint(sketch, "E191", {"position": v(-5.42, 25.49) * mm});
            skPoint(sketch, "E192", {"position": v(-1.47, 25.52) * mm});
            skPoint(sketch, "E193", {"position": v(1.54, 25.55) * mm});
            skPoint(sketch, "E194", {"position": v(4.54, 25.55) * mm});
            skPoint(sketch, "E195", {"position": v(8.27, 25.55) * mm});
            skPoint(sketch, "E196", {"position": v(11.78, 25.55) * mm});
            skPoint(sketch, "E197", {"position": v(15.59, 25.55) * mm});
            skPoint(sketch, "E198", {"position": v(18.58, 24.28) * mm});
            skPoint(sketch, "E199", {"position": v(19.29, 20.89) * mm});
            skPoint(sketch, "E200", {"position": v(19.34, 17.49) * mm});
            skPoint(sketch, "E201", {"position": v(19.44, 14.65) * mm});
            skPoint(sketch, "E202", {"position": v(19.38, 12.8) * mm});
            skPoint(sketch, "E203", {"position": v(19, 11.46) * mm});
            skPoint(sketch, "E204", {"position": v(18.03, 10.85) * mm});
            skPoint(sketch, "E205", {"position": v(-18.43, 5.59) * mm});
            skPoint(sketch, "E206", {"position": v(-18.59, 4.4) * mm});
            skPoint(sketch, "E207", {"position": v(-18.27, 6.9) * mm});
            skPoint(sketch, "E208", {"position": v(-18.72, 3.34) * mm});
            skPoint(sketch, "E209", {"position": v(-19.42, 21.13) * mm});
            skPoint(sketch, "E210", {"position": v(-19.08, 23.37) * mm});
            skFitSpline(sketch, "E211", {"points": [v(-18.82, 2.4) * mm, v(-18.72, 3.34) * mm, v(-18.59, 4.4) * mm, v(-18.43, 5.59) * mm, v(-18.27, 6.9) * mm, v(-17.98, 8.43) * mm, v(-17.95, 10.07) * mm, v(-18.46, 11.06) * mm, v(-19.23, 11.9) * mm, v(-19.48, 13.83) * mm], "startDerivative": vector(1.12, 9.9) * mm, "endDerivative": vector(-0.8, 18.24) * mm});
            skFitSpline(sketch, "E212", {"points": [v(-19.48, 13.83) * mm, v(-19.55, 16.03) * mm, v(-19.52, 18.88) * mm, v(-19.42, 21.13) * mm, v(-19.08, 23.37) * mm, v(-17.47, 25.14) * mm, v(-14.48, 25.45) * mm, v(-10.38, 25.45) * mm, v(-5.42, 25.49) * mm, v(-1.47, 25.52) * mm, v(1.54, 25.55) * mm, v(4.54, 25.55) * mm, v(8.27, 25.55) * mm, v(11.78, 25.55) * mm, v(15.59, 25.55) * mm, v(18.58, 24.28) * mm, v(19.29, 20.89) * mm, v(19.34, 17.49) * mm, v(19.44, 14.65) * mm, v(19.38, 12.8) * mm, v(19, 11.46) * mm, v(18.03, 10.85) * mm, v(17.74, 9.92) * mm], "startDerivative": vector(-2.07, 51.22) * mm, "endDerivative": vector(15.28, -45.9) * mm});
            skSolve(sketch);
        }
        {
            var Q0;
            Q0 = qSketchRegion(id + "F12", true);
            extrude(context, id + "F13", {"entities" : qUnion([Q0]), "operationType" : NewBodyOperationType.ADD, "depth" : 1 * mm, "offsetDistance" : 25 * mm});
        }
    });
